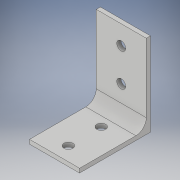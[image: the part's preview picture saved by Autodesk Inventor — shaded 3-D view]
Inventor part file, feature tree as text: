
AUTODESK INVENTOR PART (.ipt)
format: ipt  version: 2019 (Build 230136000, 136)  size: 142,336 bytes
history: native  units: in
note: dims shown in document units (in); Inventor stores cm internally (conversion verified against a paired STEP export)
features: extrude x4, sketch x4, fillet x1
ambient origin geometry x8: Origin, YZ Plane, XZ Plane, XY Plane, X Axis, Y Axis, Z Axis, Center Point
bodies: Solid1 (feature_tree)
feature tree (9):
  extrude  "Extrusion1"  Depth=0.6in
  extrude  "Extrusion2"  Depth=0.05in
  extrude  "Extrusion3"  Depth=0.8in
  fillet  "Fillet1"  Radius=0.107in
  sketch  "Sketch1"  dims[d0=1.0in d1=0.6in]
  sketch  "Sketch2"  dims[d2=0.05in d3=0.0in d4=0.05in]
  sketch  "Sketch3"  dims[d5=0.8in d6=0.0in d7=0.107in d8=0.107in]
  sketch  "Sketch4"  dims[d9=0.3in d10=0.3in d11=0.394in d12=0.377in d13=1.0in d14=0.0in d15=0.107in d17=0.394in d19=0.107in d22=0.0in d23=1.0in d24=0.125in d25=0.3in d26=0.3in]
  extrude  "Extrusion4"  Depth=0.125in
